# Revit family: FU_Stool_Sandler_Woodlook 3-12
name_source: partatom
category: Furniture
units: mm (PartAtom-declared; Revit-internal decimal feet)

## family parameters
Always vertical = Yes
Cut with Voids When Loaded = No
OmniClass Number = 23.40.20.00
OmniClass Title = General Furniture and Specialties
Room Calculation Point = No
Shared = No
Work Plane-Based = No

## types (1)
- FU_Stool_Sandler_Woodlook 3-12
    Default Elevation = 0 mm  [stored 0 ft]
    Depth = 410 mm  [stored 1.34514 ft]
    Description = Woodlook barstool with frame manufactured entirely from aluminum but with realistic appearance of wood. Highly durable and scratch resistant.
    Height = 785 mm  [stored 2.57546 ft]
    Manufacturer = Sandler
    Model = Woodlook 3.12
    Seat Depth = 420 mm  [stored 1.37795 ft]
    Seat Width = 420 mm  [stored 1.37795 ft]
    URL = https://www.sandlerseating.com
    Upholstery = Woodlook Vinyl - Dream
    Width = 410 mm  [stored 1.34514 ft]
    Woodlook = Woodlook - 21A Teak

note: [stored X ft] marks values corroborated as IEEE doubles in the binary element streams (Revit-internal decimal feet)

## geometry (parser evidence)
native form markers: Sweep x3
no freeform markers — native parametric forms only
